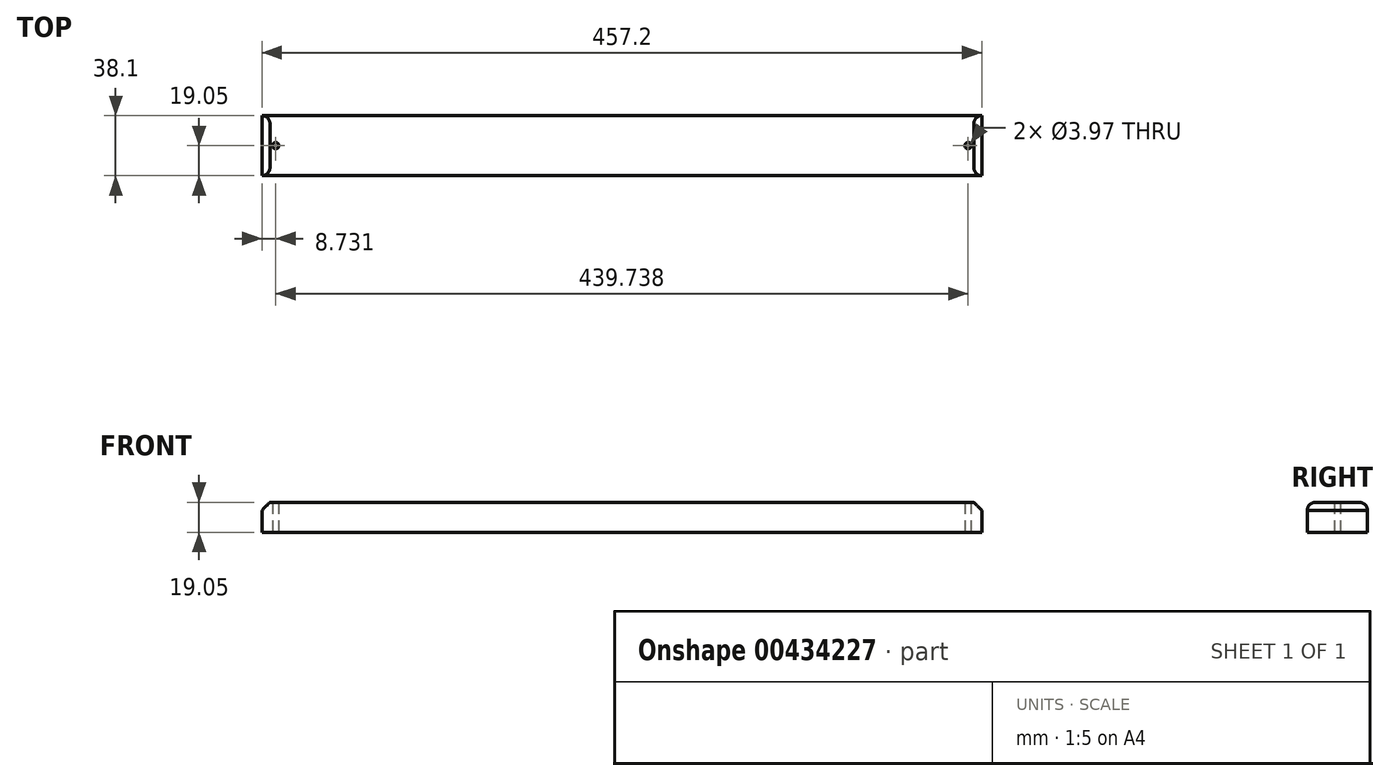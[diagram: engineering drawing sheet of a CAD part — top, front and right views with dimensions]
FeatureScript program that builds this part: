
annotation { "Feature Type Name" : "Feature", "Feature Type Description" : "" }
export const myFeature = defineFeature(function(context is Context, id is Id, definition is map)
    precondition{}
    {
        {
            var Q0;
            Q0=qCreatedBy(makeId("Top.planeOp"),FACE);
            var sketch = newSketch(context, id + "F0", { "sketchPlane" : qUnion([Q0])});
            skLineSegment(sketch, "E0.bottom", {"start": v(0, 0) * mm, "end": v(457.2, 0) * mm});
            skLineSegment(sketch, "E0.top", {"start": v(0, 38.1) * mm, "end": v(457.2, 38.1) * mm});
            skLineSegment(sketch, "E0.left", {"start": v(0, 0) * mm, "end": v(0, 38.1) * mm});
            skLineSegment(sketch, "E0.right", {"start": v(457.2, 0) * mm, "end": v(457.2, 38.1) * mm});
            skCircle(sketch, "E1", {"center": v(8.73, 19.05) * mm, "radius": 1.98 * mm});
            skLineSegment(sketch, "E2", {"start": v(228.6, 55.2) * mm, "end": v(228.6, -40.25) * mm, "construction": true});
            skPoint(sketch, "E2.startSnap0", {"position": v(228.6, 38.1) * mm});
            skCircle(sketch, "E3.MirrorC", {"center": v(448.47, 19.05) * mm, "radius": 1.98 * mm});
            skLineSegment(sketch, "E4", {"start": v(17.46, 45.5) * mm, "end": v(17.46, -18) * mm, "construction": true});
            skSolve(sketch);
        }
        {
            var Q0;
            Q0 = qSketchRegion(id + "F0", true);
            extrude(context, id + "F1", {"entities" : qUnion([Q0]), "depth" : 19.05 * mm});
        }
        {
            var Q0;
            Q0=makeQuery(id+"F1.opExtrude","CAP_EDGE",EDGE,{"disambiguationData":[OSD([sQuery(id+"F0.wireOp",EDGE,"E0.left")])],"isStart":false});
            var Q1;
            Q1=makeQuery(id+"F1.opExtrude","CAP_EDGE",EDGE,{"disambiguationData":[OSD([sQuery(id+"F0.wireOp",EDGE,"E0.right")])],"isStart":false});
            chamfer(context, id + "F2", {"entities" : qUnion([Q0, Q1]), "width" : 5.08 * mm, "tangentPropagation" : true});
        }
        {
            var Q0;
            Q0=makeQuery(id+"F1.opExtrude","CAP_EDGE",EDGE,{"disambiguationData":[OSD([sQuery(id+"F0.wireOp",EDGE,"E0.top")])],"isStart":false});
            var Q1;
            Q1=makeQuery(id+"F1.opExtrude","CAP_EDGE",EDGE,{"disambiguationData":[OSD([sQuery(id+"F0.wireOp",EDGE,"E0.bottom")])],"isStart":false});
            fillet(context, id + "F3", {"entities" : qUnion([Q0, Q1]), "radius" : 5.08 * mm, "tangentPropagation" : true, "allowEdgeOverflow" : false});
        }
    });
